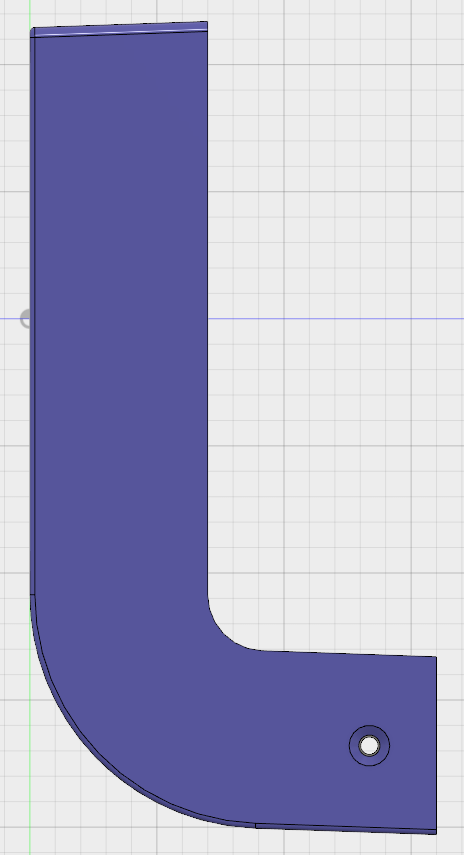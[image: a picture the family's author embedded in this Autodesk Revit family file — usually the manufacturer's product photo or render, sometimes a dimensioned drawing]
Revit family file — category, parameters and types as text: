
# Revit family: 0047952 Sylvania Lighting Fixture START eco Bollard L-Shape L IP54 570lm 830 BLK
name_source: partatom
category: Lighting Fixtures
revit_build: Autodesk Revit 2016 (Build: 20150220_1215(x64)
units: mm (PartAtom-declared; Revit-internal decimal feet)

## family parameters
Cut with Voids When Loaded = No
Host = Face
Light Source = Yes
OmniClass Number = 23.80.70.11.17
OmniClass Title = Specialized Lighting by Location or Use
Part Type = Normal
Room Calculation Point = No
Round Connector Dimension = Use Diameter
Shared = No

## types (1)
- START eco Bollard L-Shape L IP54 570lm 830 BLK
    Apparent Load = 8 VA
    Assembly Code = D5020200
    Body Material = Aluminum_Sylvania_Velite_Black
    Catalog Number = 0047952 START eco Bollard L-Shape L IP54 570lm 830 BLK
    Color Filter = 16777215
    Default Elevation = 0 mm  [stored 0 ft]
    Description = A range of sleek and stylish Outdoor LED luminaires.Velite is perfect for lighting courtyards, gardens and exterior entrances.Design  meets IK05 requirements.Available in various shapes, sizes and colours of die cast aluminium luminaires.Range includes bollards and various wall mounted direct and direct/indirect luminaires.High efficient thermal design: ta -20 to +45oC.High performance: delivers up to 830 lm (luminaire lumen output), and up to 71lm/W (total system efficiency).Available in warm white (3,000K).Energy class: A++, A+, A.Lifetime: 30,000 hours life at 70% of the original output L70.
    Diffuser Material = Polycarbonate_Sylvania_Velite_Clear
    Dimming Lamp Color Temperature Shift = <None>
    Drive Current = 300mA
    Electrical Protection = CLASS I
    Energy Class = A++ A+ A
    Height = 800 mm  [stored 2.62467 ft]
    IK Rating = IK05
    IP Rating = IP54
    Lamp = LED
    Lamp Comments = Integrated LED
    Length = 90 mm  [stored 0.295276 ft]
    Life = 25 000h
    Manufacturer = Feilo Sylvania
    Model = START eco Bollard L-Shape L IP54 570lm 830 BLK
    Photometric Web File = 0047952.ies
    Product Page URL = http://www.sylvania-lighting.com
    Ta Rating = -20°C to +45°C
    Tilt Angle = 90.00°
    URL = http://www.sylvania-lighting.com
    Voltage = 240 V
    Voltage Comments = UNV (Universal Voltage; 230-240 Volt)
    Weight = 2.07 kg
    Width = 35 mm  [stored 0.114829 ft]

note: [stored X ft] marks values corroborated as IEEE doubles in the binary element streams (Revit-internal decimal feet)

## geometry (parser evidence)
native form markers: Blend x5, Sweep x4
no freeform markers — native parametric forms only
